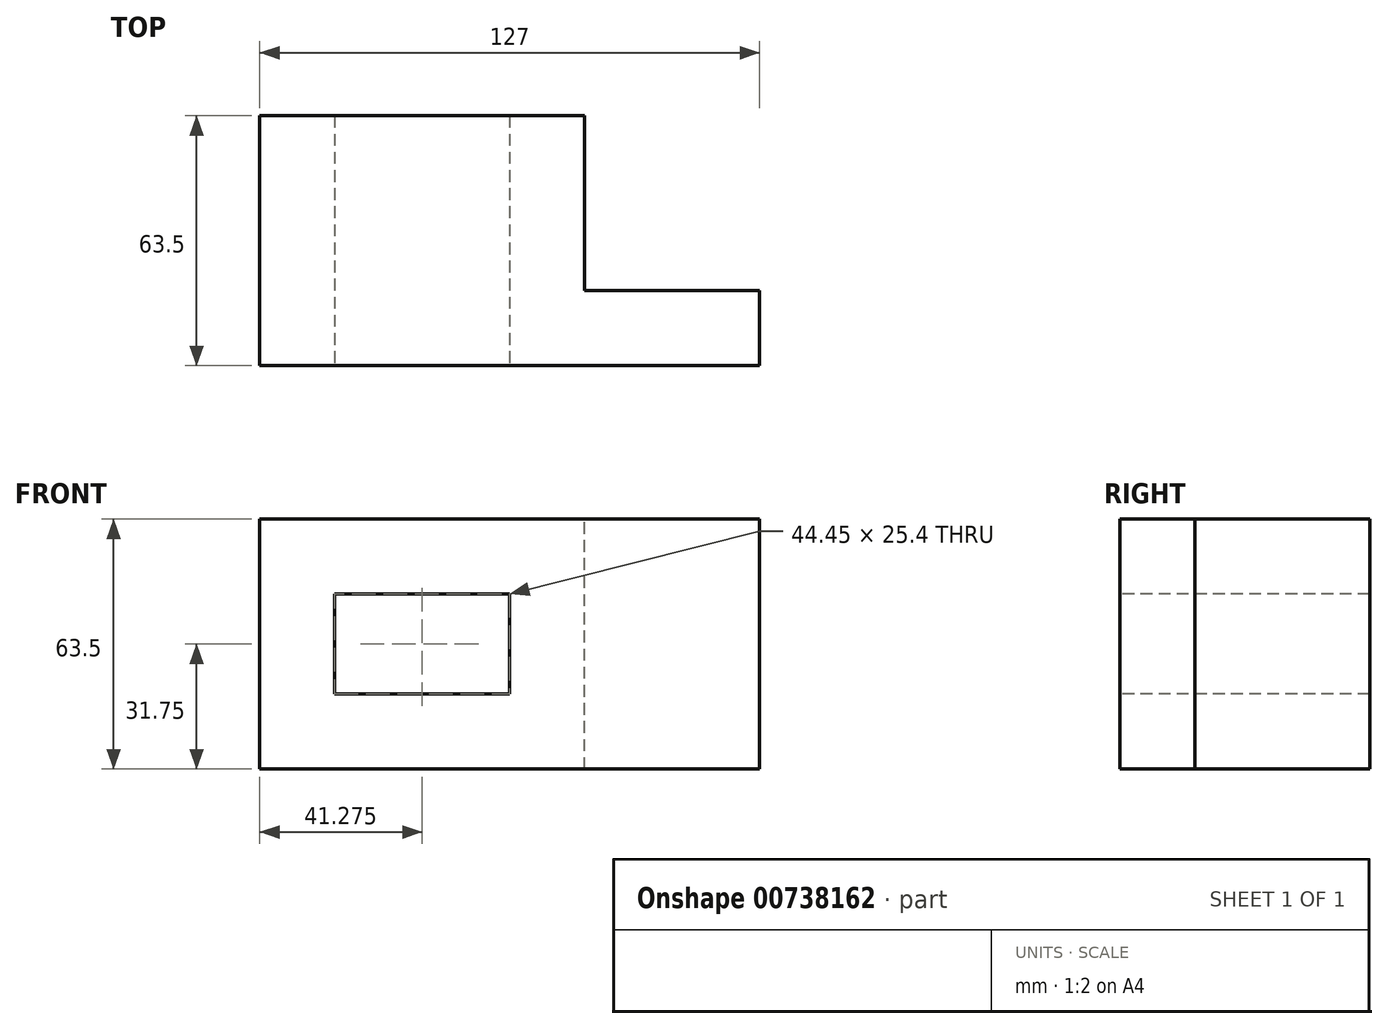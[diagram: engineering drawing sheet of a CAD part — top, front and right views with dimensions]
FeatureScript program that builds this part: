
annotation { "Feature Type Name" : "Feature", "Feature Type Description" : "" }
export const myFeature = defineFeature(function(context is Context, id is Id, definition is map)
    precondition{}
    {
        {
            var Q0;
            Q0=qCreatedBy(makeId("Front.planeOp"),FACE);
            var sketch = newSketch(context, id + "F0", { "sketchPlane" : qUnion([Q0])});
            skLineSegment(sketch, "E0.bottom", {"start": v(0, 0) * mm, "end": v(127, 0) * mm});
            skLineSegment(sketch, "E0.top", {"start": v(0, -63.5) * mm, "end": v(127, -63.5) * mm});
            skLineSegment(sketch, "E0.left", {"start": v(0, 0) * mm, "end": v(0, -63.5) * mm});
            skLineSegment(sketch, "E0.right", {"start": v(127, 0) * mm, "end": v(127, -63.5) * mm});
            skSolve(sketch);
        }
        {
            var Q0;
            Q0=makeQuery(id+"F0.imprint","IMPRINT",FACE,{"disambiguationData":[TD([[makeQuery(id+"F0.imprint","IMPRINT",EDGE,{"derivedFrom":sQuery(id+"F0.wireOp",EDGE,"E0.bottom")}),-1.0]])]});
            extrude(context, id + "F1", {"entities" : qUnion([Q0]), "depth" : 63.5 * mm, "offsetDistance" : 25.4 * mm});
        }
        {
            var Q0;
            Q0=makeQuery(id+"F1.opExtrude","CAP_FACE",FACE,{"disambiguationData":[OSD([sQuery(id+"F0.wireOp",EDGE,"E0.bottom"),sQuery(id+"F0.wireOp",EDGE,"E0.top"),sQuery(id+"F0.wireOp",EDGE,"E0.left"),sQuery(id+"F0.wireOp",EDGE,"E0.right")])],"isStart":false});
            var sketch = newSketch(context, id + "F2", { "sketchPlane" : qUnion([Q0])});
            skLineSegment(sketch, "E1.bottom", {"start": v(19.05, -19.05) * mm, "end": v(63.5, -19.05) * mm});
            skLineSegment(sketch, "E1.top", {"start": v(19.05, -44.45) * mm, "end": v(63.5, -44.45) * mm});
            skLineSegment(sketch, "E1.left", {"start": v(19.05, -19.05) * mm, "end": v(19.05, -44.45) * mm});
            skLineSegment(sketch, "E1.right", {"start": v(63.5, -19.05) * mm, "end": v(63.5, -44.45) * mm});
            skSolve(sketch);
        }
        {
            var Q0;
            Q0=makeQuery(id+"F2.imprint","IMPRINT",FACE,{"disambiguationData":[TD([[makeQuery(id+"F2.imprint","IMPRINT",EDGE,{"derivedFrom":sQuery(id+"F2.wireOp",EDGE,"E1.bottom")}),-1.0]])]});
            extrude(context, id + "F3", {"entities" : qUnion([Q0]), "operationType" : NewBodyOperationType.REMOVE, "endBound" : BoundingType.THROUGH_ALL, "oppositeDirection" : true, "depth" : 25.4 * mm, "offsetDistance" : 25.4 * mm});
        }
        {
            var Q0;
            Q0=makeQuery(id+"F1.opExtrude","SWEPT_FACE",FACE,{"disambiguationData":[OSD([sQuery(id+"F0.wireOp",EDGE,"E0.bottom")])]});
            var sketch = newSketch(context, id + "F4", { "sketchPlane" : qUnion([Q0])});
            skLineSegment(sketch, "E2.bottom", {"start": v(127, 0) * mm, "end": v(82.55, 0) * mm});
            skLineSegment(sketch, "E2.top", {"start": v(127, -44.45) * mm, "end": v(82.55, -44.45) * mm});
            skLineSegment(sketch, "E2.left", {"start": v(127, 0) * mm, "end": v(127, -44.45) * mm});
            skLineSegment(sketch, "E2.right", {"start": v(82.55, 0) * mm, "end": v(82.55, -44.45) * mm});
            skSolve(sketch);
        }
        {
            var Q0;
            Q0=makeQuery(id+"F4.imprint","IMPRINT",FACE,{"disambiguationData":[TD([[makeQuery(id+"F4.imprint","IMPRINT",EDGE,{"derivedFrom":sQuery(id+"F4.wireOp",EDGE,"E2.bottom")}),-1.0]])]});
            extrude(context, id + "F5", {"entities" : qUnion([Q0]), "operationType" : NewBodyOperationType.REMOVE, "endBound" : BoundingType.THROUGH_ALL, "oppositeDirection" : true, "depth" : 25.4 * mm, "offsetDistance" : 25.4 * mm});
        }
    });
